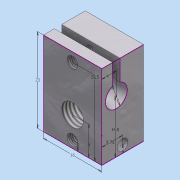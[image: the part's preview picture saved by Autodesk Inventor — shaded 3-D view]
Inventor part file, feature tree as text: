
AUTODESK INVENTOR PART (.ipt)
format: ipt  version: 2016 (Build 200138000, 138)  size: 155,136 bytes
history: native  units: mm
features: hole x4, thread x4, sketch x2, extrude x2
ambient origin geometry x8: Origin, YZ Plane, XZ Plane, XY Plane, X Axis, Y Axis, Z Axis, Center Point
bodies: Solid1 (feature_tree)
feature tree (12):
  sketch  "Sketch1"  dims[d0=16.0mm d1=23.0mm]
  extrude  "Extrusion1"  Depth=23.0mm
  hole  "Hole1"  [1 undecoded]
  hole  "Hole2"  [1 undecoded]
  hole  "Hole3"  [1 undecoded]
  sketch  "Sketch3"  dims[d3=8.0mm d4=2.0mm d5=20.5mm d6=11.5mm d7=0.0mm d8=6.0mm d9=6.0mm d10=4.0mm d11=2.0mm d12=90.0deg d13=8.0mm d14=20.594885mm d15=3.0mm d16=6.0mm d17=4.0mm d18=2.0mm d19=90.0deg d20=8.0mm d21=20.594885mm d22=3.0mm d23=6.0mm d24=4.0mm d25=2.0mm d26=90.0deg d27=6.0mm d28=20.594885mm d29=6.0mm d30=4.0mm d31=14.5mm d32=2.0mm d33=5.75mm d34=20.0mm d35=0.0mm d36=3.0mm d37=6.0mm d38=4.0mm d39=2.0mm d40=90.0deg d41=8.0mm d42=20.594885mm d43=10.0mm d44=0.0mm d45=10.0mm d46=0.0mm d47=10.0mm d48=0.0mm d49=10.0mm d50=0.0mm]
  extrude  "Extrusion2"  Depth=10.0mm
  hole  "Hole4"  [1 undecoded]
  thread  "Thread1"  [1 undecoded]
  thread  "Thread2"  [1 undecoded]
  thread  "Thread3"  [1 undecoded]
  thread  "Thread4"  [1 undecoded]
note: 8 required parameter values undecoded (feature->parameter linkage not recoverable at this tier; creation-order binding heuristic only, values carry confidence <= 0.55)
